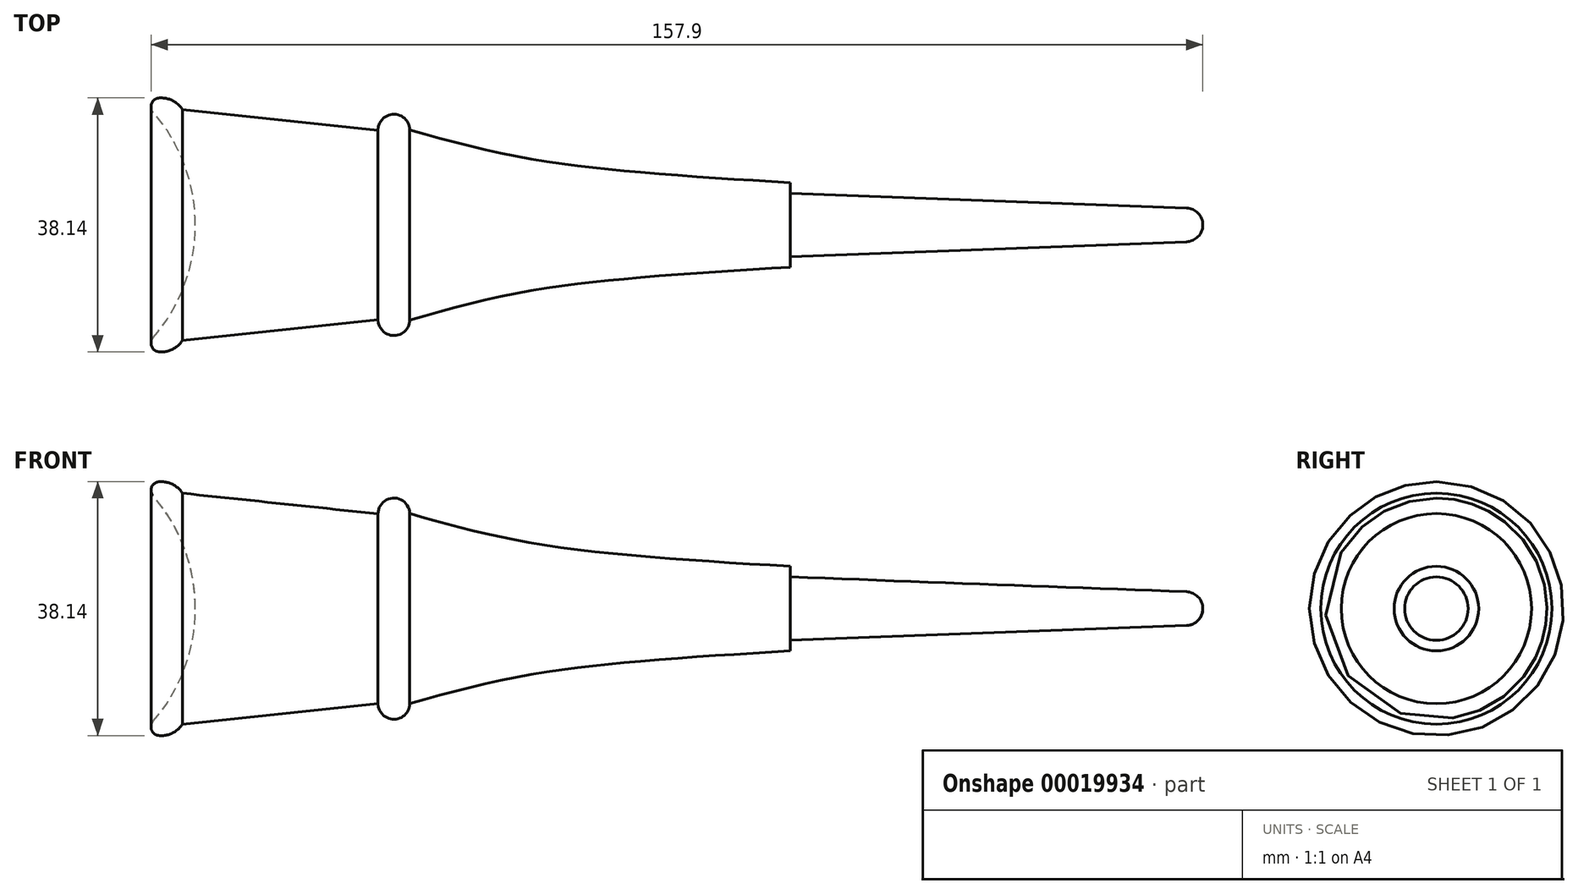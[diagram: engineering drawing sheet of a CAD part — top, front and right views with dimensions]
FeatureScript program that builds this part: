
annotation { "Feature Type Name" : "Feature", "Feature Type Description" : "" }
export const myFeature = defineFeature(function(context is Context, id is Id, definition is map)
    precondition{}
    {
        {
            var Q0;
            Q0=qCreatedBy(makeId("Front.planeOp"),FACE);
            var sketch = newSketch(context, id + "F0", { "sketchPlane" : qUnion([Q0])});
            skLineSegment(sketch, "E0.bottom", {"start": v(134.81, 0) * mm, "end": v(72.9, 0) * mm});
            skLineSegment(sketch, "E0.top", {"start": v(132.37, 2.54) * mm, "end": v(72.9, 4.76) * mm});
            skLineSegment(sketch, "E0.left", {"start": v(134.81, 0) * mm, "end": v(134.81, 0) * mm});
            skLineSegment(sketch, "E0.right", {"start": v(72.9, 0) * mm, "end": v(72.9, 4.76) * mm, "construction": true});
            skPoint(sketch, "E1.visualSharp", {"position": v(134.81, 2.45) * mm});
            skArc(sketch, "E1.filletArc", {"start": v(134.81, 0) * mm, "mid": v(134.1, 1.76) * mm, "end": v(132.37, 2.54) * mm});
            skLineSegment(sketch, "E2", {"start": v(0, 0) * mm, "end": v(0, 15.4) * mm, "construction": true});
            skLineSegment(sketch, "E3", {"start": v(72.9, 4.76) * mm, "end": v(72.9, 6.35) * mm});
            skFitSpline(sketch, "E4", {"points": [v(72.9, 6.35) * mm, v(35.23, 9.67) * mm, v(15.75, 14.29) * mm], "startDerivative": vector(-70.52, 4.23) * mm, "endDerivative": vector(-42.3, 12.05) * mm});
            skArc(sketch, "E5", {"start": v(15.75, 14.29) * mm, "mid": v(13.34, 16.62) * mm, "end": v(10.99, 14.23) * mm});
            skLineSegment(sketch, "E6", {"start": v(-18.38, 17.34) * mm, "end": v(10.99, 14.23) * mm});
            skArc(sketch, "E7", {"start": v(-18.38, 17.34) * mm, "mid": v(-19.93, 18.7) * mm, "end": v(-21.96, 19.05) * mm});
            skArc(sketch, "E8", {"start": v(-16.45, 0) * mm, "mid": v(-18.08, 9.05) * mm, "end": v(-22.78, 16.95) * mm});
            skPoint(sketch, "E9.end.orphan", {"position": v(-16.45, 0) * mm});
            skPoint(sketch, "E9.start.orphan", {"position": v(-23.94, 0) * mm});
            skPoint(sketch, "E10.visualSharp", {"position": v(-23.95, 18.21) * mm});
            skArc(sketch, "E10.filletArc", {"start": v(-21.96, 19.05) * mm, "mid": v(-23, 18.25) * mm, "end": v(-22.78, 16.95) * mm});
            skLineSegment(sketch, "E11", {"start": v(-16.45, 0) * mm, "end": v(134.81, 0) * mm});
            skSolve(sketch);
        }
        {
            var Q0;
            Q0=makeQuery(id+"F0.imprint","IMPRINT",FACE,{"disambiguationData":[TD([[makeQuery(id+"F0.imprint","IMPRINT",EDGE,{"derivedFrom":sQuery(id+"F0.wireOp",EDGE,"E0.top")}),1.0]])]});
            var Q1;
            Q1=sQuery(id+"F0.wireOp",EDGE,"E11");
            revolve(context, id + "F1", {"entities" : qUnion([Q0]), "axis" : qUnion([Q1]), "revolveType" : RevolveType.FULL});
        }
    });
